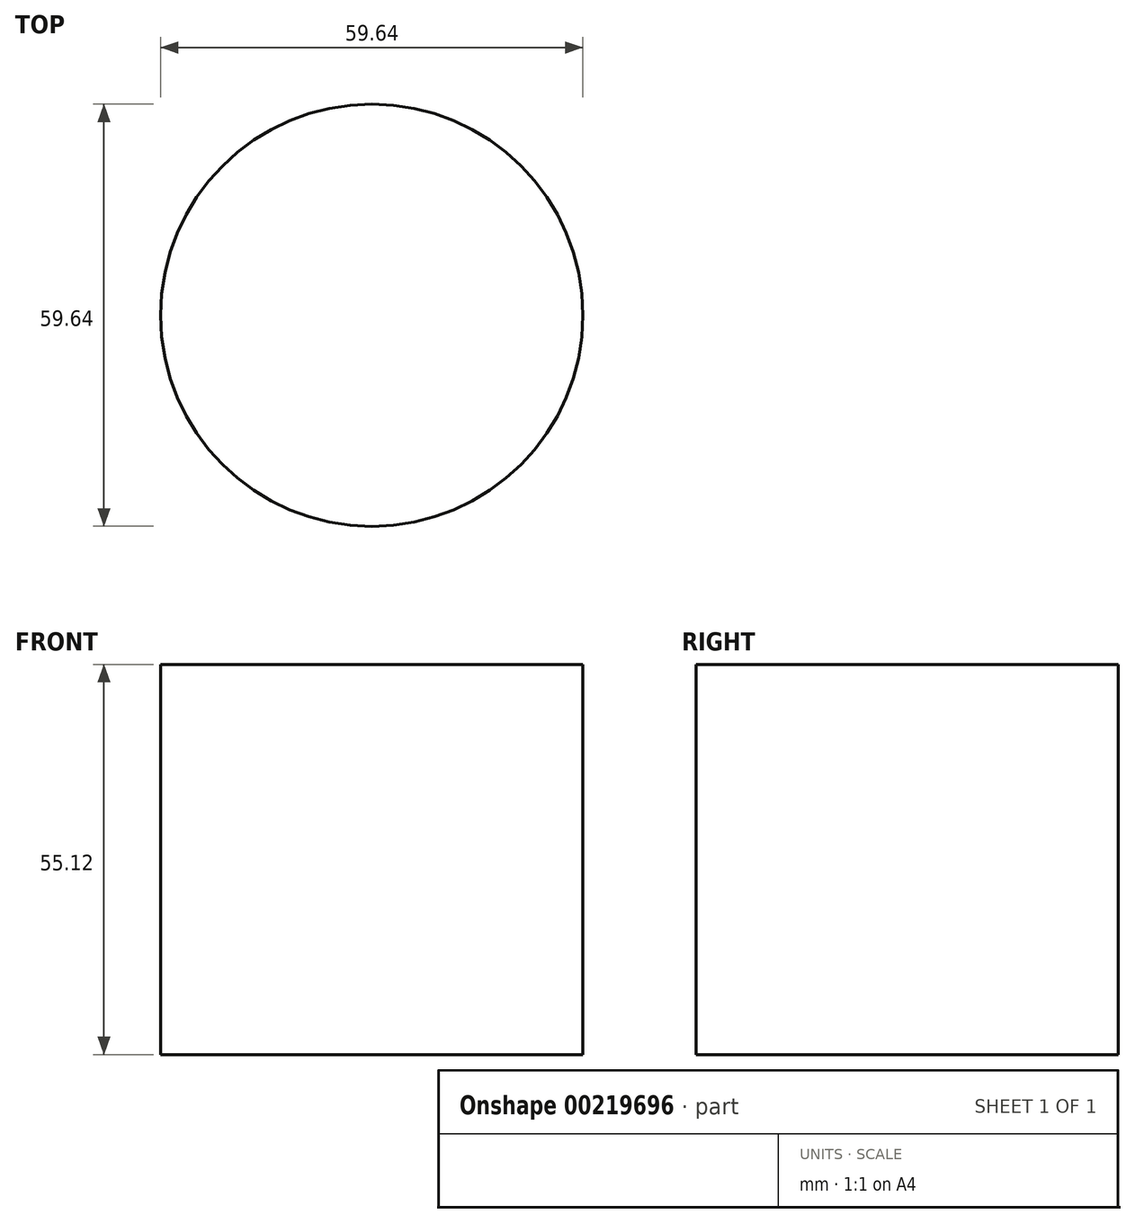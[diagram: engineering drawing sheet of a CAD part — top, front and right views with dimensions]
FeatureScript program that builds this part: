
annotation { "Feature Type Name" : "Feature", "Feature Type Description" : "" }
export const myFeature = defineFeature(function(context is Context, id is Id, definition is map)
    precondition{}
    {
        {
            var Q0;
            Q0=qCreatedBy(makeId("Top.planeOp"),FACE);
            var sketch = newSketch(context, id + "F0", { "sketchPlane" : qUnion([Q0])});
            skCircle(sketch, "E0", {"center": v(-37.6, 38.33) * mm, "radius": 29.82 * mm});
            skLineSegment(sketch, "E1.bottom", {"start": v(11.95, 61.94) * mm, "end": v(66.46, 61.94) * mm});
            skLineSegment(sketch, "E1.top", {"start": v(11.95, -55.23) * mm, "end": v(66.46, -55.23) * mm});
            skLineSegment(sketch, "E1.left", {"start": v(11.95, 61.94) * mm, "end": v(11.95, -55.23) * mm});
            skLineSegment(sketch, "E1.right", {"start": v(66.46, 61.94) * mm, "end": v(66.46, -55.23) * mm});
            skLineSegment(sketch, "E2", {"start": v(-63.25, -55.23) * mm, "end": v(-42.85, -8.9) * mm});
            skLineSegment(sketch, "E3", {"start": v(-42.85, -8.9) * mm, "end": v(-24.2, -54.36) * mm});
            skLineSegment(sketch, "E4", {"start": v(-24.2, -54.36) * mm, "end": v(-63.25, -55.23) * mm});
            skSolve(sketch);
        }
        {
            var Q0;
            Q0=sQuery(id+"F0.wireOp",EDGE,"E0");
            extrude(context, id + "F1", {"bodyType" : ToolBodyType.SURFACE, "surfaceEntities" : qUnion([Q0]), "oppositeDirection" : true, "depth" : 55.12 * mm});
        }
    });
